# Revit family: SANINDUSA_107722004_Waterline_showertray100x80_V0
name_source: partatom
category: Plumbing Fixtures
revit_build: Autodesk Revit 2018 (Build: 20170223_1515(x64)
units: mm (PartAtom-declared; Revit-internal decimal feet)

## family parameters
Cut with Voids When Loaded = No
Host = Face
Part Type = Normal
Room Calculation Point = No
Round Connector Dimension = Use Diameter
Shared = No

## types (1)
- SANINDUSA_107722004_Waterline_showertray100x80_V0
    AssetType = Fixed
    CodePerformance = EN 14527:2006 / A1:2010 CL 2
    Color = white
    Constituents = 48711-90 shower tray drain (not included)
    Default Elevation = 1219 mm
    Description = Installation or waste water appliance that emits a spray of water to wash the human body (BS6100)
    DrainSize = 90 mm  [stored 0.295276 ft]
    Element Type = SHOWER: Installation or waste water appliance that emits a spray of water to wash the human body (BS6100)
    Features = Wide range of sizes adaptable to different spaces; Extra flat shower tray makes shower access easier for all users; Offers the ultimate in contemporary bathroom design.
    Finish = gloss
    HasTray = TRUE
    Installation Instructions = https://www.tec.sanindusa.pt
    Manufacturer = Sanindusa
    ManufacturerName = Sanindusa
    ManufacturerURL = www.tec.sanindusa.pt
    Material = Fine Fireclay
    Model = 107722004
    ModelNumber = 107722004
    ModelReference = Waterline
    MountingType = AboveTheFloor
    Name = 100x80x5 Waterline shower tray
    NominalDepth = 25 mm  [stored 0.082021 ft]
    NominalHeight = 45 mm  [stored 0.147638 ft]
    NominalLength = 1000 mm  [stored 3.28084 ft]
    NominalWidth = 800 mm  [stored 2.62467 ft]
    Non-slip surface = FALSE
    ProductInformation = https://www.tec.sanindusa.pt
    ProductionYear = 2018
    Shape = rectangular
    ShowerType = Other
    Size = 100x80
    URL = www.tec.sanindusa.pt
    WarrantyDescription = https://www.tec.sanindusa.pt
    WarrantyDurationParts = 5
    Waste Connection = Yes
    Weight = 33.80 kg

note: [stored X ft] marks values corroborated as IEEE doubles in the binary element streams (Revit-internal decimal feet)

## geometry (parser evidence)
native form markers: Sweep x6
no freeform markers — native parametric forms only
